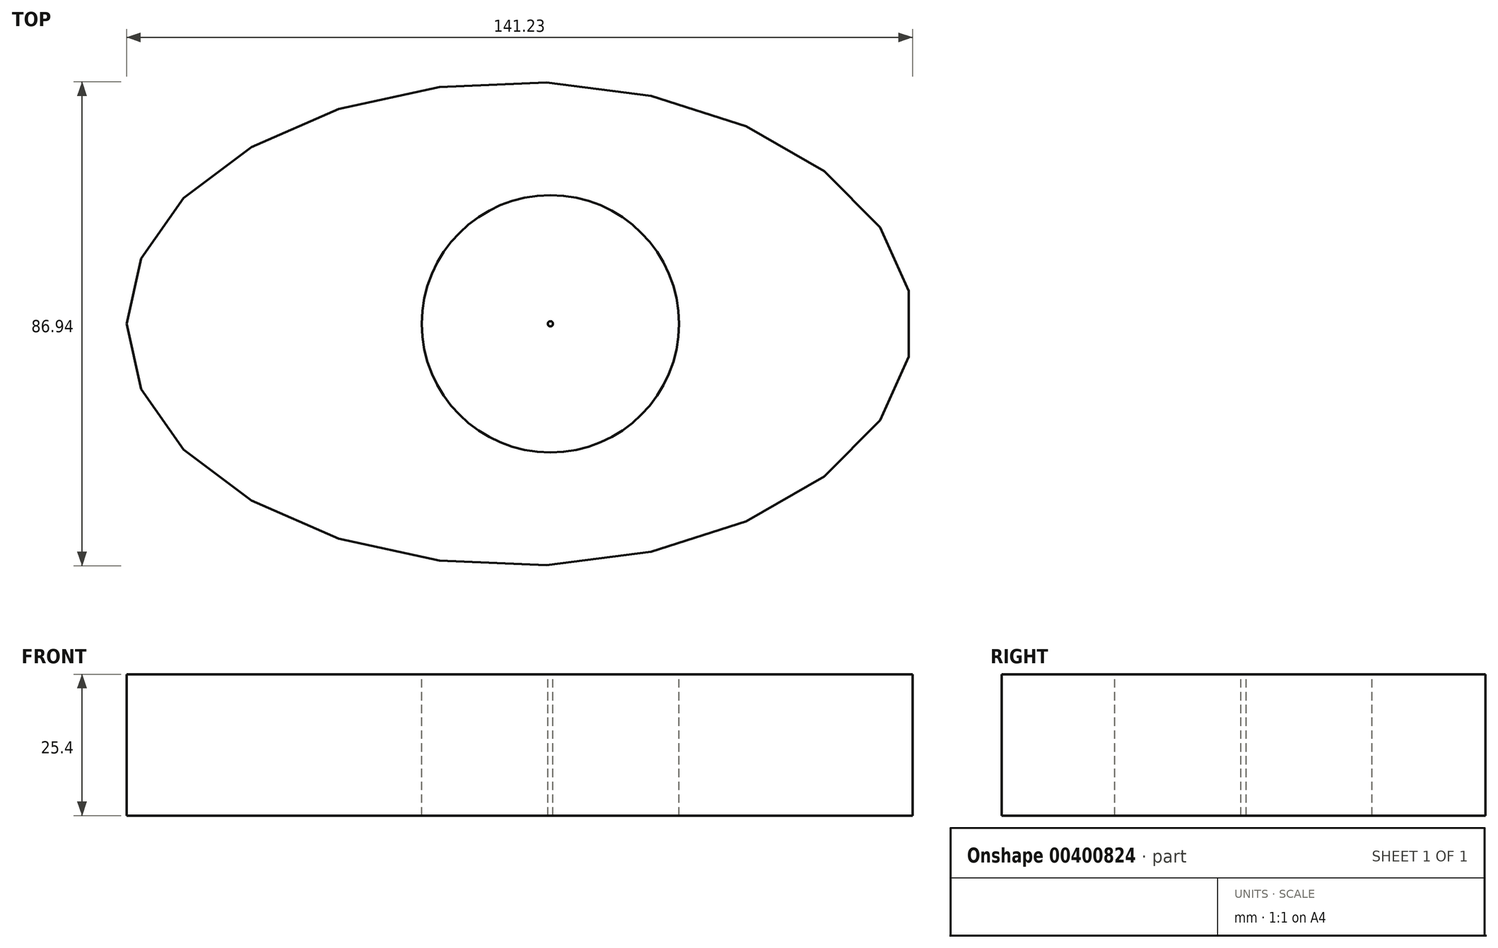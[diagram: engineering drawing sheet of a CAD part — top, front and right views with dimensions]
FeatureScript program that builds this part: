
annotation { "Feature Type Name" : "Feature", "Feature Type Description" : "" }
export const myFeature = defineFeature(function(context is Context, id is Id, definition is map)
    precondition{}
    {
        {
            var Q0;
            Q0=qCreatedBy(makeId("Top.planeOp"),FACE);
            var sketch = newSketch(context, id + "F0", { "sketchPlane" : qUnion([Q0])});
            skEllipse(sketch, "E0", {"center": v(70.61, 0) * mm, "majorRadius": 70.61 * mm, "minorRadius": 43.47 * mm, "majorAxis": v(-1, 0)});
            skSolve(sketch);
        }
        {
            var Q0;
            Q0=makeQuery(id+"F0.imprint","IMPRINT",FACE,{"disambiguationData":[TD([[makeQuery(id+"F0.imprint","IMPRINT",EDGE,{"derivedFrom":sQuery(id+"F0.wireOp",EDGE,"E0")}),1.0]])]});
            var sketch = newSketch(context, id + "F1", { "sketchPlane" : qUnion([Q0])});
            skCircle(sketch, "E1", {"center": v(76.16, 0) * mm, "radius": 0.46 * mm});
            skCircle(sketch, "E2", {"center": v(76.16, 0) * mm, "radius": 23.12 * mm});
            skSolve(sketch);
        }
        {
            var Q0;
            Q0=sQuery(id+"F1.wireOp",EDGE,"E2");
            var Q1;
            Q1=sQuery(id+"F1.wireOp",EDGE,"E1");
            extrude(context, id + "F2", {"bodyType" : ToolBodyType.SURFACE, "surfaceEntities" : qUnion([Q0, Q1]), "depth" : 25.4 * mm});
        }
        {
            var Q0;
            Q0=sQuery(id+"F0.wireOp",EDGE,"E0");
            extrude(context, id + "F3", {"bodyType" : ToolBodyType.SURFACE, "surfaceEntities" : qUnion([Q0]), "depth" : 25.4 * mm});
        }
    });
